# Revit family: HOSPITAIR 2 15 bar
name_source: partatom
category: Equipement de génie climatique
revit_build: Autodesk Revit 2018 (Build: 20190510_1515(x64)
units: mm (PartAtom-declared; Revit-internal decimal feet)

## family parameters
Basée sur le plan de construction = Non
Classification = Aucun
Cote de connecteur circulaire = Utiliser le diamètre
Couper avec des vides une fois chargée = Non
Partagée = Non
Point de calcul de pièce = Non
Toujours verticalement = Oui
Type d'élément = Normal

## types (6) — shared parameters
BRANCHEMENT_TERRE = Oui
COS_PHI = 0.9
DIAM_REFOUL_AIR = 15 mm  [stored 0.0492126 ft]
DOUBLE_ALIMENTATION = Oui
HAUTEUR_SORTIE AIR = 968 mm
LONGUEUR_SORTIE AIR = 747 mm  [stored 2.45079 ft]
NBR_POLES = 3
NEUTRE = Oui
TENSION_ALIM = 400 V
Zone de Maintenance = 600 mm  [stored 1.9685 ft]
Zone de maintenance = Non
Zone de maintenance_Hauteur = 1565 mm  [stored 5.13451 ft]

## per-type parameters (varying)
| type | 12 K2 R5 | 20-27 K2 R5 | CAPOT HAUEUR | COMPRESSEUR K2 | Cuve + structure (Standard ou capotée) | DEPLACEMENT EQUERRE COFFRET | DESCR_ALIM_X | DESCR_ALIM_Y | DESCR_REFOUL_AIR | Debit_refoulement_air | NIVEAU_SONORE(dB(A)) | POIDS(Kg) | POMPE 12 K2 R5_HAUTEUR | POMPE 20-27 K2 R5_HAUTEUR | PUISS_APPARENTE | PUISS_ELECT | Version Capotée |
| 12 K2 R5 - CAPOTÉE | Oui | Non | 1455 mm  [stored 4.77362 ft] | COMPRESSEUR 12 K2 R5 : 12 K2 R5 - CAPOTÉ | HOSPITAIR 2 15 bar - CUVE + STRUCTURE : HOSPITAIR SCROLAIR 2 - CUVE + STRUCTURE (Moteurs capotés) | 270 mm  [stored 0.885827 ft] | Alimentation électrique, 5G2.5mm² | Alimentation électrique, 5G2.5mm² | Refoulement Air; 22m3/h; G1/2"FEM | 22.0 m³/h | 62 | 880 mm | 915 mm  [stored 3.00197 ft] | 915 mm  [stored 3.00197 ft] | 1889 VA | 2 kW | Oui |
| 12 K2 R5 - NON CAPOTÉE | Oui | Non | 1455 mm  [stored 4.77362 ft] | COMPRESSEUR 12 K2 R5 : 12 K2 R5 - STANDARD | HOSPITAIR 2 15 bar - CUVE + STRUCTURE : HOSPITAIR SCROLAIR 2 - CUVE + STRUCTURE (Standard) | 265 mm  [stored 0.869423 ft] | Alimentation électrique, 5G2.5mm² | Alimentation électrique, 5G2.5mm² | Refoulement Air; 22m3/h; G1/2"FEM | 22.0 m³/h | 71 | 550 mm | 810 mm | 810 mm | 1889 VA | 2 kW | Non |
| 20 K2 R5 - CAPOTÉE | Non | Oui | 1545 mm | COMPRESSEUR 12 K2 R5 : 12 K2 R5 - CAPOTÉ | HOSPITAIR 2 15 bar - CUVE + STRUCTURE : HOSPITAIR SCROLAIR 2 - CUVE + STRUCTURE (Moteurs capotés) | 270 mm  [stored 0.885827 ft] | Alimentation électrique, 5G4mm² | Alimentation électrique, 5G4mm² | Refoulement Air; 40m3/h; G1/2"FEM | 40.0 m³/h | 67 | 880 mm | 915 mm  [stored 3.00197 ft] | 915 mm  [stored 3.00197 ft] | 3333 VA | 3 kW | Oui |
| 27 K2 R5 - CAPOTÉE | Non | Oui | 1545 mm | COMPRESSEUR 12 K2 R5 : 20 K2 R5 - CAPOTÉ | HOSPITAIR 2 15 bar - CUVE + STRUCTURE : HOSPITAIR SCROLAIR 2 - CUVE + STRUCTURE (Moteurs capotés) | 270 mm  [stored 0.885827 ft] | Alimentation électrique, 5G4mm² | Alimentation électrique, 5G4mm² | Refoulement Air; 54m3/h; G1/2"FEM | 54.0 m³/h | 68 | 910 mm | 915 mm  [stored 3.00197 ft] | 915 mm  [stored 3.00197 ft] | 4444 VA | 4 kW | Oui |
| 20 K2 R5 - NON CAPOTÉE | Non | Oui | 1545 mm | COMPRESSEUR 12 K2 R5 : 20 K2 R5 - STANDARD | HOSPITAIR 2 15 bar - CUVE + STRUCTURE : HOSPITAIR SCROLAIR 2 - CUVE + STRUCTURE (Standard) | 265 mm  [stored 0.869423 ft] | Alimentation électrique, 5G4mm² | Alimentation électrique, 5G4mm² | Refoulement Air; 40m3/h; G1/2"FEM | 40.0 m³/h | 75 | 550 mm | 810 mm | 810 mm | 3333 VA | 3 kW | Non |
| 27 K2 R5 - NON CAPOTÉE | Non | Oui | 1545 mm | COMPRESSEUR 12 K2 R5 : 27 K2 R5 - STANDARD | HOSPITAIR 2 15 bar - CUVE + STRUCTURE : HOSPITAIR SCROLAIR 2 - CUVE + STRUCTURE (Standard) | 265 mm  [stored 0.869423 ft] | Alimentation électrique, 5G4mm² | Alimentation électrique, 5G4mm² | Refoulement Air; 54m3/h; G1/2"FEM | 54.0 m³/h | 77 | 630 mm  [stored 2.06693 ft] | 810 mm | 810 mm | 4444 VA | 4 kW | Non |

note: [stored X ft] marks values corroborated as IEEE doubles in the binary element streams (Revit-internal decimal feet)

## geometry (parser evidence)
native form markers: Sweep x12
no freeform markers — native parametric forms only
